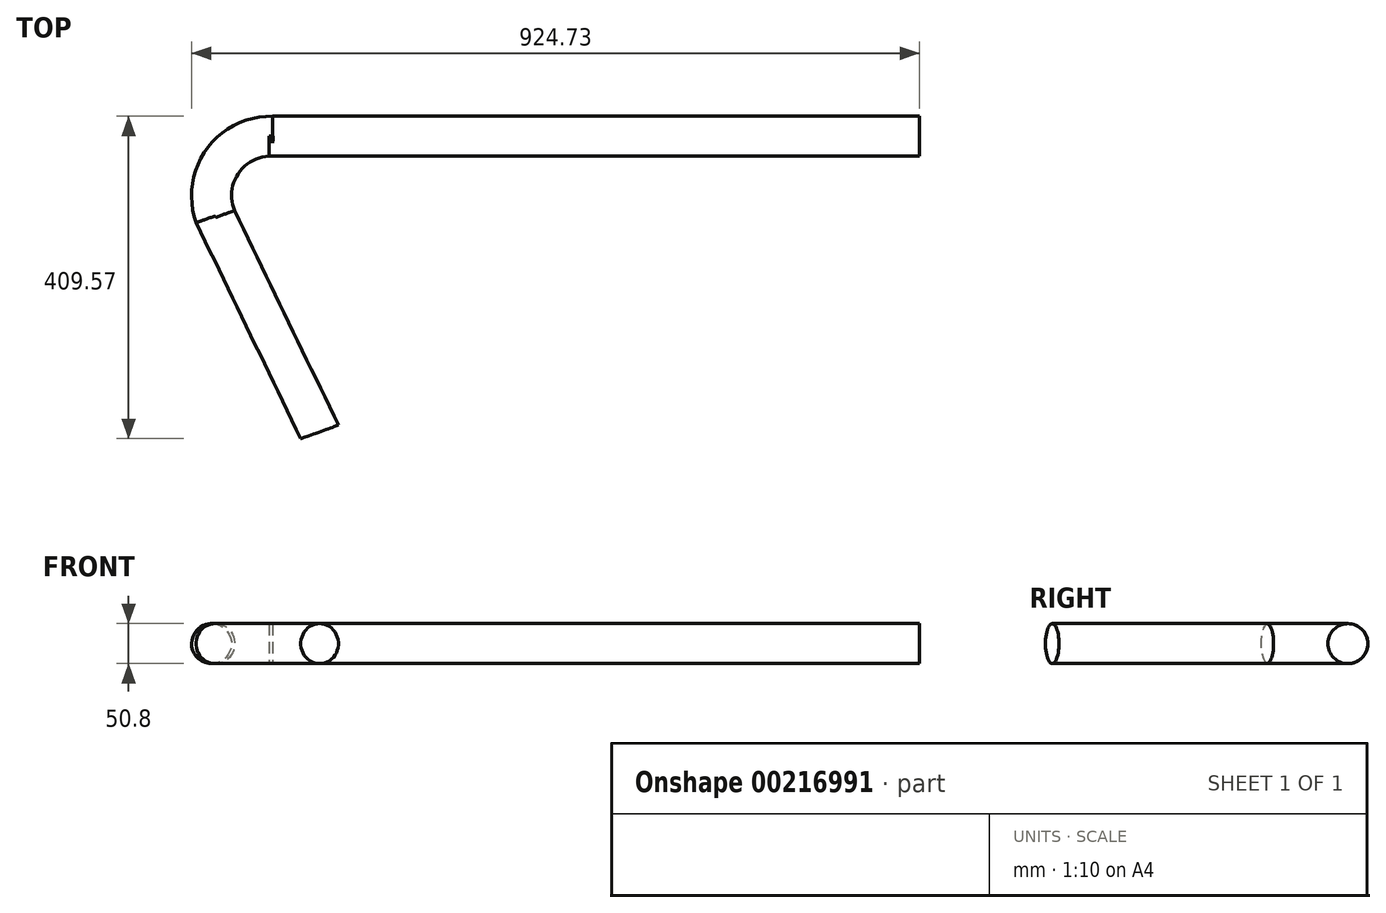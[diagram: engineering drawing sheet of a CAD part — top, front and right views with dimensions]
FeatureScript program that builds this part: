
annotation { "Feature Type Name" : "Feature", "Feature Type Description" : "" }
export const myFeature = defineFeature(function(context is Context, id is Id, definition is map)
    precondition{}
    {
        {
            var Q0;
            Q0=qCreatedBy(makeId("Top.planeOp"),FACE);
            var sketch = newSketch(context, id + "F0", { "sketchPlane" : qUnion([Q0])});
            skLineSegment(sketch, "E0", {"start": v(0, 0) * mm, "end": v(-826.44, 0) * mm});
            skLineSegment(sketch, "E1", {"start": v(-891.77, -85.4) * mm, "end": v(-836.33, -294.63) * mm});
            skArc(sketch, "E2", {"start": v(-806, 0) * mm, "mid": v(-876.47, -28.87) * mm, "end": v(-886.75, -104.34) * mm});
            skSolve(sketch);
        }
        {
            var Q0;
            Q0=qCreatedBy(makeId("Right.planeOp"),FACE);
            var sketch = newSketch(context, id + "F1", { "sketchPlane" : qUnion([Q0])});
            skCircle(sketch, "E3", {"center": v(0, 0) * mm, "radius": 25.4 * mm});
            skSolve(sketch);
        }
        {
            var Q0;
            Q0=makeQuery(id+"F1.imprint","IMPRINT",FACE,{"disambiguationData":[TD([[makeQuery(id+"F1.imprint","IMPRINT",EDGE,{"derivedFrom":sQuery(id+"F1.wireOp",EDGE,"E3")}),1.0]])]});
            var Q1;
            Q1=sQuery(id+"F0.wireOp",EDGE,"E0");
            sweep(context, id + "F2", {"profiles" : qUnion([Q0]), "path" : qUnion([Q1])});
        }
        {
            var Q0;
            Q0=qCreatedBy(makeId("Top.planeOp"),FACE);
            var sketch = newSketch(context, id + "F3", { "sketchPlane" : qUnion([Q0])});
            skArc(sketch, "E4", {"start": v(-820.93, 0.87) * mm, "mid": v(-886.17, -31.16) * mm, "end": v(-894.89, -103.31) * mm});
            skLineSegment(sketch, "E5", {"start": v(-899.4, -86.5) * mm, "end": v(-820.32, -380.86) * mm});
            skLineSegment(sketch, "E6", {"start": v(-827.14, 0.87) * mm, "end": v(-678.88, 0.87) * mm});
            skSolve(sketch);
        }
        {
            var Q0;
            Q0=makeQuery(id+"F2.opSweep","CAP_FACE",FACE,{"disambiguationData":[OSD([sQuery(id+"F0.wireOp",VERTEX,"E0.end"),sQuery(id+"F1.wireOp",EDGE,"E3")])],"isStart":false});
            var Q1;
            Q1=sQuery(id+"F3.wireOp",EDGE,"E4");
            sweep(context, id + "F4", {"operationType" : NewBodyOperationType.ADD, "profiles" : qUnion([Q0]), "path" : qUnion([Q1])});
        }
        {
            var Q0;
            Q0=qCreatedBy(makeId("Top.planeOp"),FACE);
            var sketch = newSketch(context, id + "F5", { "sketchPlane" : qUnion([Q0])});
            skLineSegment(sketch, "E7", {"start": v(-894.6, -101.12) * mm, "end": v(-761.74, -375.44) * mm});
            skSolve(sketch);
        }
        {
            var Q0;
            Q0=makeQuery(id+"F4.opSweep","CAP_FACE",FACE,{"disambiguationData":[OSD([sQuery(id+"F0.wireOp",VERTEX,"E0.end"),sQuery(id+"F1.wireOp",EDGE,"E3"),sQuery(id+"F3.wireOp",VERTEX,"E4.end")])],"isStart":false});
            var Q1;
            Q1=sQuery(id+"F5.wireOp",EDGE,"E7");
            sweep(context, id + "F6", {"operationType" : NewBodyOperationType.ADD, "profiles" : qUnion([Q0]), "path" : qUnion([Q1])});
        }
    });
